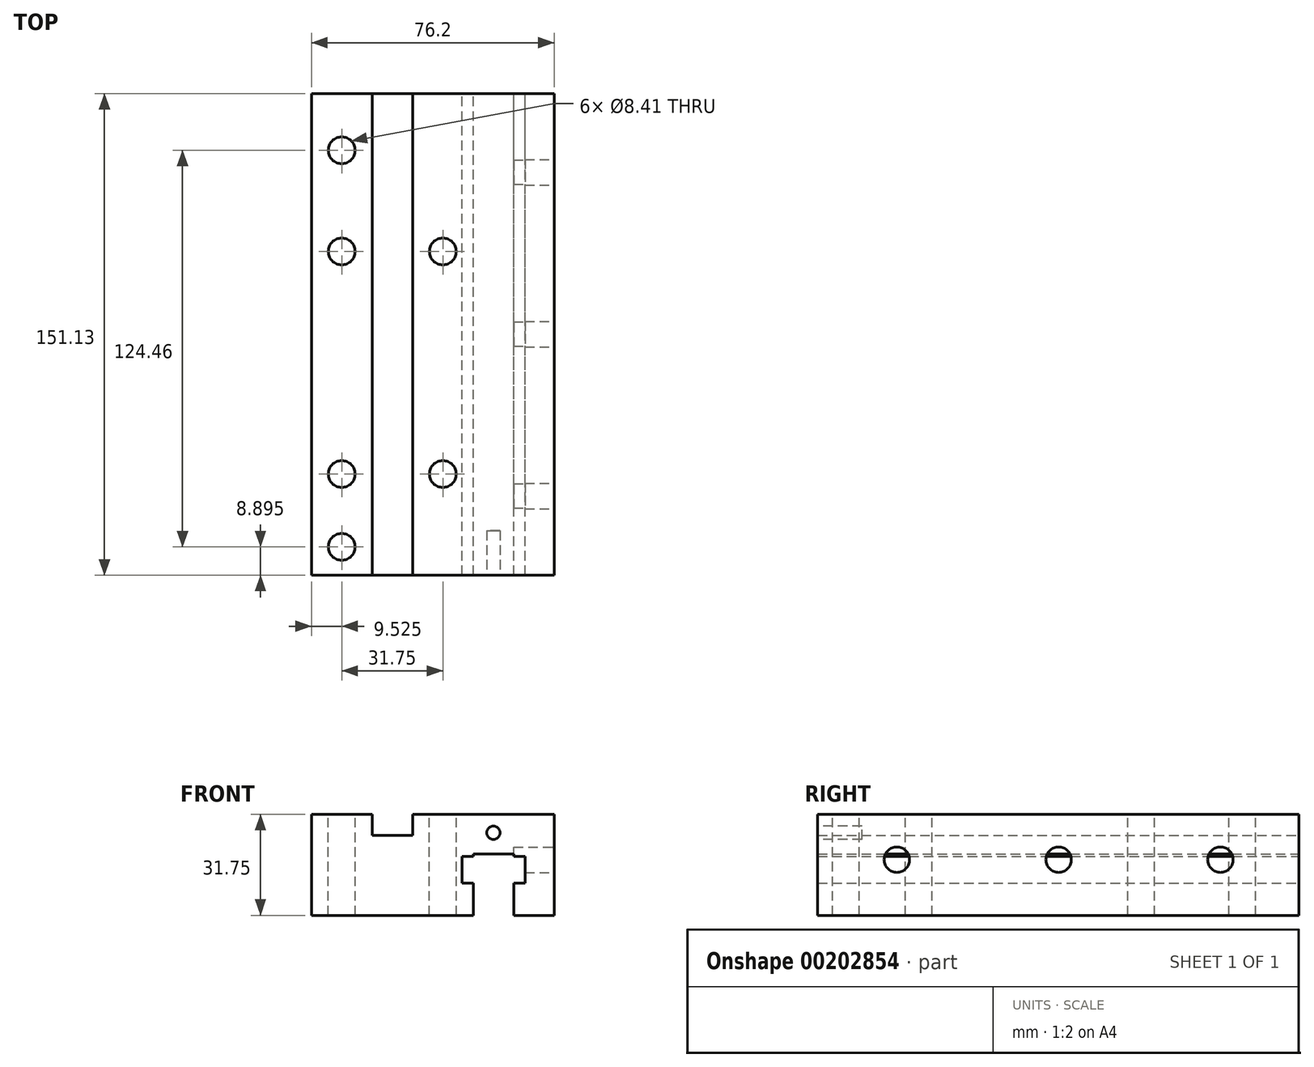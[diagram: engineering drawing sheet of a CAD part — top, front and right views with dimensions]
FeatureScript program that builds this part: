
annotation { "Feature Type Name" : "Feature", "Feature Type Description" : "" }
export const myFeature = defineFeature(function(context is Context, id is Id, definition is map)
    precondition{}
    {
        {
            var Q0;
            Q0=qCreatedBy(makeId("Front.planeOp"),FACE);
            var sketch = newSketch(context, id + "F0", { "sketchPlane" : qUnion([Q0])});
            skLineSegment(sketch, "E0", {"start": v(0, 0) * mm, "end": v(0, 31.75) * mm});
            skLineSegment(sketch, "E1", {"start": v(0, 31.75) * mm, "end": v(31.78, 31.75) * mm});
            skLineSegment(sketch, "E2", {"start": v(31.78, 31.75) * mm, "end": v(31.78, 25.15) * mm});
            skLineSegment(sketch, "E3", {"start": v(19.05, 25.15) * mm, "end": v(31.78, 25.15) * mm});
            skLineSegment(sketch, "E4", {"start": v(19.05, 25.15) * mm, "end": v(19.05, 31.75) * mm});
            skLineSegment(sketch, "E5", {"start": v(19.05, 31.75) * mm, "end": v(76.2, 31.75) * mm});
            skLineSegment(sketch, "E6", {"start": v(76.2, 31.75) * mm, "end": v(76.2, 0) * mm});
            skLineSegment(sketch, "E7", {"start": v(76.2, 0) * mm, "end": v(63.5, 0) * mm});
            skLineSegment(sketch, "E8", {"start": v(63.5, 0) * mm, "end": v(63.5, 10.16) * mm});
            skLineSegment(sketch, "E9", {"start": v(63.5, 10.16) * mm, "end": v(67.06, 10.16) * mm});
            skLineSegment(sketch, "E10", {"start": v(67.06, 10.16) * mm, "end": v(67.06, 18.54) * mm});
            skLineSegment(sketch, "E11", {"start": v(67.06, 18.54) * mm, "end": v(63.5, 18.54) * mm});
            skLineSegment(sketch, "E12", {"start": v(63.5, 18.54) * mm, "end": v(63.5, 19.3) * mm});
            skLineSegment(sketch, "E13", {"start": v(63.5, 19.3) * mm, "end": v(50.8, 19.3) * mm});
            skLineSegment(sketch, "E14", {"start": v(50.8, 19.3) * mm, "end": v(50.8, 18.54) * mm});
            skLineSegment(sketch, "E15", {"start": v(50.8, 18.54) * mm, "end": v(47.24, 18.54) * mm});
            skLineSegment(sketch, "E16", {"start": v(47.24, 18.54) * mm, "end": v(47.24, 10.16) * mm});
            skLineSegment(sketch, "E17", {"start": v(47.24, 10.16) * mm, "end": v(50.8, 10.16) * mm});
            skLineSegment(sketch, "E18", {"start": v(50.8, 10.16) * mm, "end": v(50.8, 0) * mm});
            skLineSegment(sketch, "E19", {"start": v(50.8, 0) * mm, "end": v(0, 0) * mm});
            skLineSegment(sketch, "E20", {"start": v(57.15, 36.04) * mm, "end": v(57.15, -9) * mm, "construction": true});
            skPoint(sketch, "E20.startSnap0", {"position": v(57.15, 19.3) * mm});
            skSolve(sketch);
        }
        {
            var Q0;
            Q0=makeQuery(id+"F0.imprint","IMPRINT",FACE,{"disambiguationData":[TD([[makeQuery(id+"F0.imprint","IMPRINT",EDGE,{"derivedFrom":sQuery(id+"F0.wireOp",EDGE,"E0")}),-1.0]])]});
            extrude(context, id + "F1", {"entities" : qUnion([Q0]), "endBound" : BoundingType.SYMMETRIC, "depth" : 151.13 * mm});
        }
        {
            var Q0;
            Q0=makeQuery(id+"F1.opExtrude","CAP_FACE",FACE,{"disambiguationData":[OSD([sQuery(id+"F0.wireOp",EDGE,"E0"),sQuery(id+"F0.wireOp",EDGE,"E1"),sQuery(id+"F0.wireOp",EDGE,"E2"),sQuery(id+"F0.wireOp",EDGE,"E3"),sQuery(id+"F0.wireOp",EDGE,"E4"),sQuery(id+"F0.wireOp",EDGE,"E5"),sQuery(id+"F0.wireOp",EDGE,"E6"),sQuery(id+"F0.wireOp",EDGE,"E7"),sQuery(id+"F0.wireOp",EDGE,"E8"),sQuery(id+"F0.wireOp",EDGE,"E9"),sQuery(id+"F0.wireOp",EDGE,"E10"),sQuery(id+"F0.wireOp",EDGE,"E11"),sQuery(id+"F0.wireOp",EDGE,"E12"),sQuery(id+"F0.wireOp",EDGE,"E13"),sQuery(id+"F0.wireOp",EDGE,"E14"),sQuery(id+"F0.wireOp",EDGE,"E15"),sQuery(id+"F0.wireOp",EDGE,"E16"),sQuery(id+"F0.wireOp",EDGE,"E17"),sQuery(id+"F0.wireOp",EDGE,"E18"),sQuery(id+"F0.wireOp",EDGE,"E19")])],"isStart":false});
            var sketch = newSketch(context, id + "F2", { "sketchPlane" : qUnion([Q0])});
            skCircle(sketch, "E21", {"center": v(57.15, 25.92) * mm, "radius": 2.1 * mm});
            skSolve(sketch);
        }
        {
            var Q0;
            Q0=makeQuery(id+"F2.imprint","IMPRINT",FACE,{"disambiguationData":[TD([[makeQuery(id+"F2.imprint","IMPRINT",EDGE,{"derivedFrom":sQuery(id+"F2.wireOp",EDGE,"E21")}),1.0]])]});
            extrude(context, id + "F3", {"entities" : qUnion([Q0]), "operationType" : NewBodyOperationType.REMOVE, "oppositeDirection" : true, "depth" : 13.97 * mm});
        }
        {
            var Q0;
            Q0=makeQuery(id+"F1.opExtrude","SWEPT_FACE",FACE,{"disambiguationData":[OSD([sQuery(id+"F0.wireOp",EDGE,"E6")])]});
            var sketch = newSketch(context, id + "F4", { "sketchPlane" : qUnion([Q0])});
            skCircle(sketch, "E22", {"center": v(-50.67, 17.48) * mm, "radius": 4 * mm});
            skCircle(sketch, "E23", {"center": v(0.13, 17.48) * mm, "radius": 4 * mm});
            skLineSegment(sketch, "E24", {"start": v(-50.67, 17.48) * mm, "end": v(84.25, 17.48) * mm, "construction": true});
            skCircle(sketch, "E25", {"center": v(50.93, 17.48) * mm, "radius": 4 * mm});
            skSolve(sketch);
        }
        {
            var Q0;
            Q0=makeQuery(id+"F4.imprint","IMPRINT",FACE,{"disambiguationData":[TD([[makeQuery(id+"F4.imprint","IMPRINT",EDGE,{"derivedFrom":sQuery(id+"F4.wireOp",EDGE,"E22")}),1.0]])]});
            var Q1;
            Q1=makeQuery(id+"F4.imprint","IMPRINT",FACE,{"disambiguationData":[TD([[makeQuery(id+"F4.imprint","IMPRINT",EDGE,{"derivedFrom":sQuery(id+"F4.wireOp",EDGE,"E23")}),1.0]])]});
            var Q2;
            Q2=makeQuery(id+"F4.imprint","IMPRINT",FACE,{"disambiguationData":[TD([[makeQuery(id+"F4.imprint","IMPRINT",EDGE,{"derivedFrom":sQuery(id+"F4.wireOp",EDGE,"E25")}),1.0]])]});
            var Q3;
            Q3=makeQuery(id+"F1.opExtrude","SWEPT_BODY",BODY,{"disambiguationData":[OSD([sQuery(id+"F0.wireOp",EDGE,"E0"),sQuery(id+"F0.wireOp",EDGE,"E1"),sQuery(id+"F0.wireOp",EDGE,"E2"),sQuery(id+"F0.wireOp",EDGE,"E3"),sQuery(id+"F0.wireOp",EDGE,"E4"),sQuery(id+"F0.wireOp",EDGE,"E5"),sQuery(id+"F0.wireOp",EDGE,"E6"),sQuery(id+"F0.wireOp",EDGE,"E7"),sQuery(id+"F0.wireOp",EDGE,"E8"),sQuery(id+"F0.wireOp",EDGE,"E9"),sQuery(id+"F0.wireOp",EDGE,"E10"),sQuery(id+"F0.wireOp",EDGE,"E11"),sQuery(id+"F0.wireOp",EDGE,"E12"),sQuery(id+"F0.wireOp",EDGE,"E13"),sQuery(id+"F0.wireOp",EDGE,"E14"),sQuery(id+"F0.wireOp",EDGE,"E15"),sQuery(id+"F0.wireOp",EDGE,"E16"),sQuery(id+"F0.wireOp",EDGE,"E17"),sQuery(id+"F0.wireOp",EDGE,"E18"),sQuery(id+"F0.wireOp",EDGE,"E19")])]});
            extrude(context, id + "F5", {"entities" : qUnion([Q0, Q1, Q2]), "operationType" : NewBodyOperationType.REMOVE, "oppositeDirection" : true, "endBoundEntityBody" : qUnion([Q3]), "depth" : 12.7 * mm});
        }
        {
            var Q0;
            Q0=makeQuery(id+"F1.opExtrude","SWEPT_FACE",FACE,{"disambiguationData":[OSD([sQuery(id+"F0.wireOp",EDGE,"E1")])]});
            var sketch = newSketch(context, id + "F6", { "sketchPlane" : qUnion([Q0])});
            skCircle(sketch, "E26", {"center": v(9.52, 26.04) * mm, "radius": 4.2 * mm});
            skCircle(sketch, "E27", {"center": v(9.52, 57.79) * mm, "radius": 4.2 * mm});
            skCircle(sketch, "E28", {"center": v(9.53, -43.82) * mm, "radius": 4.2 * mm});
            skCircle(sketch, "E29", {"center": v(9.53, -66.68) * mm, "radius": 4.2 * mm});
            skLineSegment(sketch, "E30", {"start": v(9.52, 57.79) * mm, "end": v(9.53, -66.68) * mm, "construction": true});
            skCircle(sketch, "E31", {"center": v(41.27, 26.04) * mm, "radius": 4.2 * mm});
            skCircle(sketch, "E32", {"center": v(41.28, -43.82) * mm, "radius": 4.2 * mm});
            skSolve(sketch);
        }
        {
            var Q0;
            Q0=makeQuery(id+"F6.imprint","IMPRINT",FACE,{"disambiguationData":[TD([[makeQuery(id+"F6.imprint","IMPRINT",EDGE,{"derivedFrom":sQuery(id+"F6.wireOp",EDGE,"E27")}),1.0]])]});
            var Q1;
            Q1=makeQuery(id+"F6.imprint","IMPRINT",FACE,{"disambiguationData":[TD([[makeQuery(id+"F6.imprint","IMPRINT",EDGE,{"derivedFrom":sQuery(id+"F6.wireOp",EDGE,"E26")}),1.0]])]});
            var Q2;
            Q2=makeQuery(id+"F6.imprint","IMPRINT",FACE,{"disambiguationData":[TD([[makeQuery(id+"F6.imprint","IMPRINT",EDGE,{"derivedFrom":sQuery(id+"F6.wireOp",EDGE,"E31")}),1.0]])]});
            var Q3;
            Q3=makeQuery(id+"F6.imprint","IMPRINT",FACE,{"disambiguationData":[TD([[makeQuery(id+"F6.imprint","IMPRINT",EDGE,{"derivedFrom":sQuery(id+"F6.wireOp",EDGE,"E32")}),1.0]])]});
            var Q4;
            Q4=makeQuery(id+"F6.imprint","IMPRINT",FACE,{"disambiguationData":[TD([[makeQuery(id+"F6.imprint","IMPRINT",EDGE,{"derivedFrom":sQuery(id+"F6.wireOp",EDGE,"E28")}),1.0]])]});
            var Q5;
            Q5=makeQuery(id+"F6.imprint","IMPRINT",FACE,{"disambiguationData":[TD([[makeQuery(id+"F6.imprint","IMPRINT",EDGE,{"derivedFrom":sQuery(id+"F6.wireOp",EDGE,"E29")}),1.0]])]});
            extrude(context, id + "F7", {"entities" : qUnion([Q0, Q1, Q2, Q3, Q4, Q5]), "operationType" : NewBodyOperationType.REMOVE, "endBound" : BoundingType.THROUGH_ALL, "oppositeDirection" : true, "depth" : 25.4 * mm});
        }
    });
